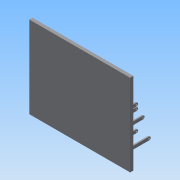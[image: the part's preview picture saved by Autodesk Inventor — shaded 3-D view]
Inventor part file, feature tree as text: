
AUTODESK INVENTOR PART (.ipt)
format: ipt  version: 2015 (Build 190159000, 159)  size: 139,776 bytes
history: native  units: mm
features: extrude x3, sketch x3, other x1
ambient origin geometry x8: Origin, YZ Plane, XZ Plane, XY Plane, X Axis, Y Axis, Z Axis, Center Point
bodies: Body1 (feature_tree)
feature tree (7):
  other  "實體1"
  extrude  "擠出1"  Depth=160.0mm
  extrude  "擠出2"  Depth=130.0mm
  extrude  "擠出3"  Depth=5.0mm TaperAngle=0.0deg
  sketch  "草圖1"
  sketch  "草圖2"
  sketch  "草圖3"
